# Revit family: Lighting-Industrial-GEWISS-SMART[4]HT_HIGHBAYS-LED_3M
name_source: partatom
category: Apparecchi per illuminazione
units: mm (PartAtom-declared; Revit-internal decimal feet)

## family parameters
Basato su piano di lavoro = Sì
Condiviso = No
Numero OmniClass = 23.80.70.00
Punto di calcolo locali = No
Quota connettore circolare = Usa diametro
Sempre verticale = No
Sorgente d'illuminazione = No
Taglio con vuoti quando caricato = No
Tipo di parte = Normale
Titolo OmniClass = Lighting

## types (8) — shared parameters
Application = Internal
Body = PA6 "Halogen Free" loaded fibreglass
Carico apparente = 194 VA
Catalogue = LIGHTING
Classification: = -
Classificazione = Lighting
Color Rendering Index = CRI-80
Colour = Grey RAL 7035
Colour : = Grey RAL 7035
Commenti sul wattaggio = 194W
Context = Logistics and industrial manufacturing lighting
Control System = ON / OFF
Control System : = ON / OFF
DIN 18032-3 certification = -
Device with reduced surface temperature = Yes
Distanza Sorg_Lum = 21 mm
Driver = Included
Driver Box = Built-in
Electrocod = 2444
Eletrical and lighting features = -
External screw = Stainless steel
Fixing = -
Gasket = anti-aging silicone
General information = -
Glow Wire Test : = 850 °C
IDF = b524b0b5-1ad1-46d1-96b9-62335af85fc8
IDT = 2b22b49849d64f60bc51ff7354190d7a
IP degree = IP66
IPEA = -
Immagine tipo = GWL1371.jpg
Installationa and maintenance = -
Insulation class = I
LED Maintenance = Non-replaceable
Lampada = LED
Larghezza = 504 mm  [stored 1.65354 ft]
Lifetime = L90B10 (Tq+25°C) = 100.000 h - L90B10 (Tq+60°C) = 50.000 h
Locking Hook = -
Luminaire = LED Industrial ReflectorÂ
Lunghezza = 700 mm  [stored 2.29659 ft]
Materials = -
Maximum surface exposed to the wind : = 0,350 m²
Mouting and installation = Ceiling - Wallmounting - Suspension
Operating temperature : = -30°C ÷ +60 °C
Optic Maintenance = Non-replaceable
Optic and illuminating features = -
Overvoltage protection = DM 6 kV / CM 10 kV
Photobiological Risk Class = RG0
Produttore = GEWISS S.p.A.
Prospetto di default = 1219 mm
Rated frequency (Hz) = 50/60 Hz
Shield type = Tempered glass Thickness 4mm
Shock resistance = IK08
Spessore plafoniera = 40 mm  [stored 0.131234 ft]
Standard Deviation Colour Matching = SDCM = 3
Standard- = EN 60598-1 ; EN 60598-2-1 ; EN 60598-2-24
Standards and approvals = -
Stocking temperature = -40 +70 °C
Supply voltage = 220 - 240 V
System power = 189W
Technical sheet = https://www.gewiss.com
Tilt- = With bracket accessory
Type of light source = LED - Not replaceable
URL = https://www.gewiss.com
Unique digital code (Datamatrix) = Datamatrix
Version file RFA = 20.11
Voltaggio = 230 V
Warranty = 5 years
Weight (kg): = 13,5
Wiring = With GW connect watertight connector

## per-type parameters (varying)
| type | Colour temperature | Descrizione | Efficiency (lm/W) | Lumen output (lm) | Modello | Optic | Optic : | SEO | Unified Glare Rating |
| GWS4420CA840 - SMART4HB 4M ST.AL.ON/OFF HT ARR.40K | 4000K | SMART[4]HB 4M ST.AL.ON/OFF HT ARR.40K | 148 | 28000 | GWS4420CA840 | Array | Metallized polycarbonate reflector | High bay | UGR - 25 |
| GWS4420CH857 - SMART4HB 4M ST.AL.ON/OFF HT 60° 57K | 5700K | SMART[4]HB 4M ST.AL.ON/OFF HT 60° 57K | 149 | 28100 | GWS4420CH857 | 60° | Metallic PC reflector and PMMA lenses |  | UGR - 19 |
| GWS4420CP857 - SMART4HB 4M ST.AL.ON/OFF HT 90° 57K | 5700K | SMART[4]HB 4M ST.AL.ON/OFF HT 90° 57K | 150 | 28300 | GWS4420CP857 | 90° | Metallic PC reflector and PMMA lenses |  | UGR - 22 |
| GWS4420CP840 - SMART4HB 4M ST.AL.ON/OFF HT 90° 40K | 4000K | SMART[4]HB 4M ST.AL.ON/OFF HT 90° 40K | 150 | 28300 | GWS4420CP840 | 90° | Metallic PC reflector and PMMA lenses |  | UGR - 22 |
| GWS4420CQ840 - SMART4HB 4M ST.AL.ON/OFF HT ELL.40K | 4000K | SMART[4]HB 4M ST.AL.ON/OFF HT ELL.40K | 133 | 25100 | GWS4420CQ840 | Elliptical | Metallic PC reflector and PMMA lenses | High bay | - |
| GWS4420CA857 - SMART4HB 4M ST.AL.ON/OFF HT ARR.57K | 5700K | SMART[4]HB 4M ST.AL.ON/OFF HT ARR.57K | 148 | 28000 | GWS4420CA857 | Array | Metallized polycarbonate reflector | High bay | UGR - 25 |
| GWS4420CH840 - SMART4HB 4M ST.AL.ON/OFF HT 60° 40K | 4000K | SMART[4]HB 4M ST.AL.ON/OFF HT 60° 40K | 149 | 28100 | GWS4420CH840 | 60° | Metallic PC reflector and PMMA lenses |  | UGR - 19 |
| GWS4420CQ857 - SMART4HB 4M ST.AL.ON/OFF HT ELL.57K | 5700K | SMART[4]HB 4M ST.AL.ON/OFF HT ELL.57K | 133 | 25100 | GWS4420CQ857 | Elliptical | Metallic PC reflector and PMMA lenses | High bay | - |

note: [stored X ft] marks values corroborated as IEEE doubles in the binary element streams (Revit-internal decimal feet)

## geometry (parser evidence)
native form markers: Sweep x1
no freeform markers — native parametric forms only
